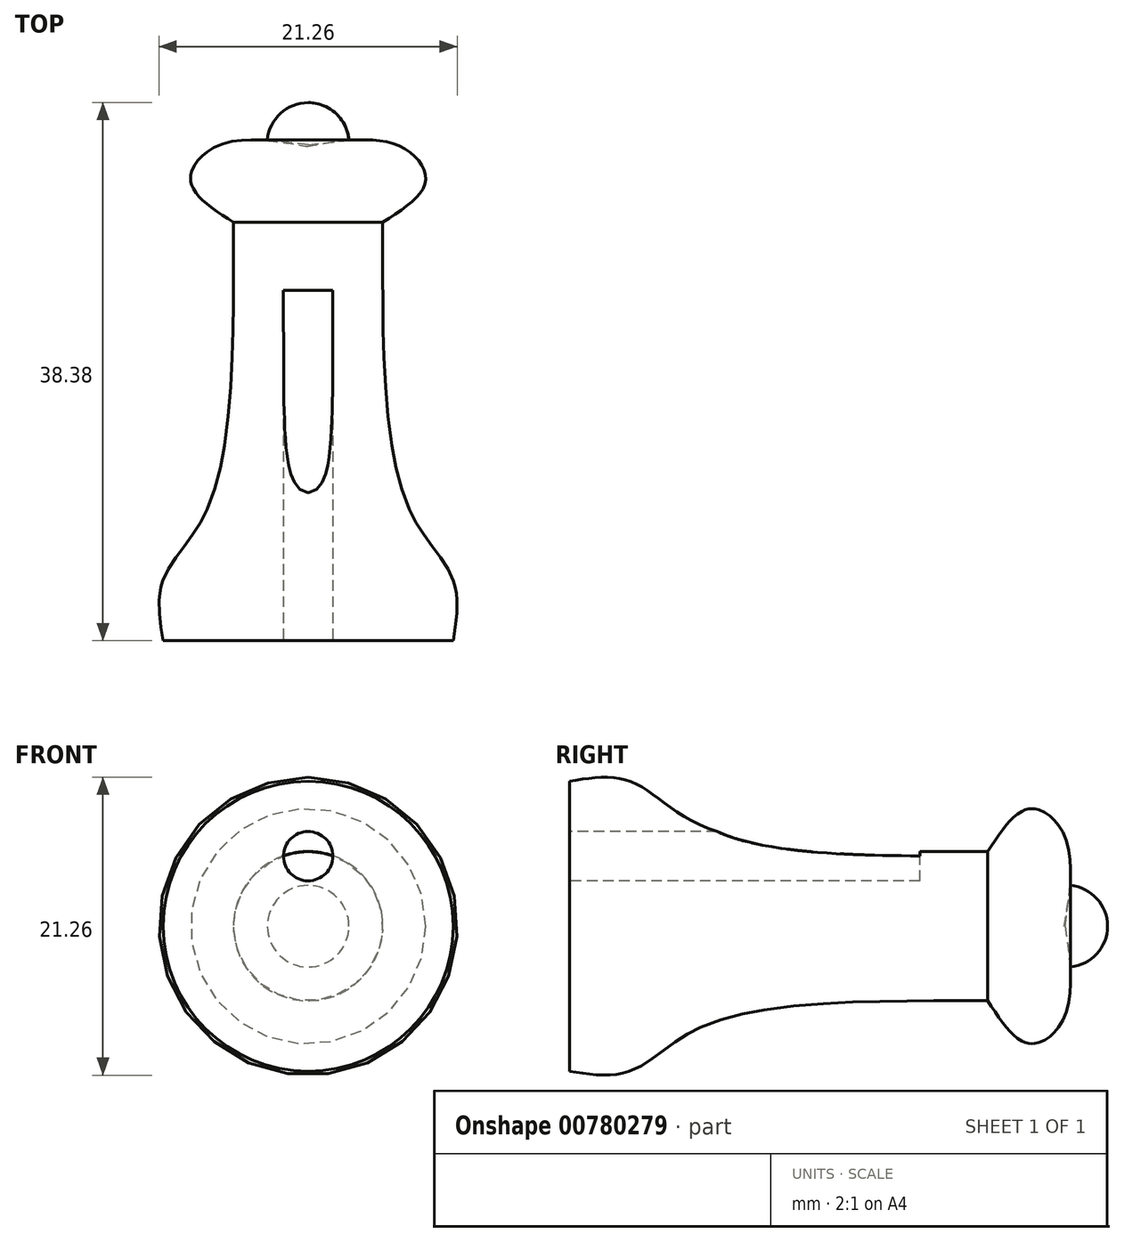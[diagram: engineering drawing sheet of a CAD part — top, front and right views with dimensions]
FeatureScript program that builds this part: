
annotation { "Feature Type Name" : "Feature", "Feature Type Description" : "" }
export const myFeature = defineFeature(function(context is Context, id is Id, definition is map)
    precondition{}
    {
        {
            var Q0;
            Q0=qCreatedBy(makeId("Top.planeOp"),FACE);
            var sketch = newSketch(context, id + "F0", { "sketchPlane" : qUnion([Q0])});
            skLineSegment(sketch, "E0", {"start": v(0, 0) * mm, "end": v(10.35, 0) * mm});
            skFitSpline(sketch, "E1", {"points": [v(10.35, 0) * mm, v(10.35, 4.32) * mm, v(7.13, 9.54) * mm, v(5.32, 29.83) * mm], "startDerivative": vector(3.17, 19.7) * mm, "endDerivative": vector(0.21, 48.08) * mm});
            skLineSegment(sketch, "E2", {"start": v(0, 35.26) * mm, "end": v(0, 0) * mm});
            skFitSpline(sketch, "E3", {"points": [v(5.32, 29.83) * mm, v(8.38, 32.8) * mm, v(6.42, 35.32) * mm, v(0, 35.26) * mm], "startDerivative": vector(13.54, 8.73) * mm, "endDerivative": vector(-17.82, -2.96) * mm});
            skSolve(sketch);
        }
        {
            var Q0;
            Q0=makeQuery(id+"F0.imprint","IMPRINT",FACE,{"disambiguationData":[TD([[makeQuery(id+"F0.imprint","IMPRINT",EDGE,{"derivedFrom":sQuery(id+"F0.wireOp",EDGE,"E0")}),1.0]])]});
            var sketch = newSketch(context, id + "F1", { "sketchPlane" : qUnion([Q0])});
            skArc(sketch, "E4", {"start": v(2.9, 35.72) * mm, "mid": v(1.96, 37.62) * mm, "end": v(-0.02, 38.38) * mm});
            skLineSegment(sketch, "E5", {"start": v(0, 35.25) * mm, "end": v(0, 32.54) * mm});
            skLineSegment(sketch, "E6", {"start": v(-0.01, 35.36) * mm, "end": v(-0.02, 38.38) * mm});
            skLineSegment(sketch, "E7", {"start": v(-0.01, 35.36) * mm, "end": v(2.9, 35.72) * mm});
            skLineSegment(sketch, "E8", {"start": v(0, 35.25) * mm, "end": v(0, 38.38) * mm});
            skSolve(sketch);
        }
        {
            var Q0;
            Q0=makeQuery(id+"F0.imprint","IMPRINT",FACE,{"disambiguationData":[TD([[makeQuery(id+"F0.imprint","IMPRINT",EDGE,{"derivedFrom":sQuery(id+"F0.wireOp",EDGE,"E0")}),1.0]])]});
            var Q1;
            Q1=sQuery(id+"F0.wireOp",EDGE,"E2");
            revolve(context, id + "F2", {"surfaceOperationType" : NewSurfaceOperationType.NEW, "entities" : qUnion([Q0]), "axis" : qUnion([Q1]), "revolveType" : RevolveType.FULL});
        }
        {
            var Q0;
            {var subQ0=sQuery(id+"F1.wireOp",EDGE,"E4");Q0=makeQuery(id+"F1.imprint","IMPRINT",FACE,{"disambiguationData":[TD([[makeQuery(id+"F1.imprint","IMPRINT",EDGE,{"derivedFrom":subQ0}),1.0]])]});}
            var Q1;
            Q1=sQuery(id+"F0.wireOp",EDGE,"E2");
            revolve(context, id + "F3", {"surfaceOperationType" : NewSurfaceOperationType.NEW, "entities" : qUnion([Q0]), "axis" : qUnion([Q1]), "revolveType" : RevolveType.FULL});
        }
        {
            var Q0;
            Q0=qCreatedBy(makeId("Front.planeOp"),FACE);
            var sketch = newSketch(context, id + "F4", { "sketchPlane" : qUnion([Q0])});
            skCircle(sketch, "E9", {"center": v(0, 5) * mm, "radius": 1.76 * mm});
            skSolve(sketch);
        }
        {
            var Q0;
            Q0 = qSketchRegion(id + "F4", true);
            extrude(context, id + "F5", {"entities" : qUnion([Q0]), "operationType" : NewBodyOperationType.REMOVE, "oppositeDirection" : true, "depth" : 25 * mm, "offsetDistance" : 25 * mm});
        }
    });
